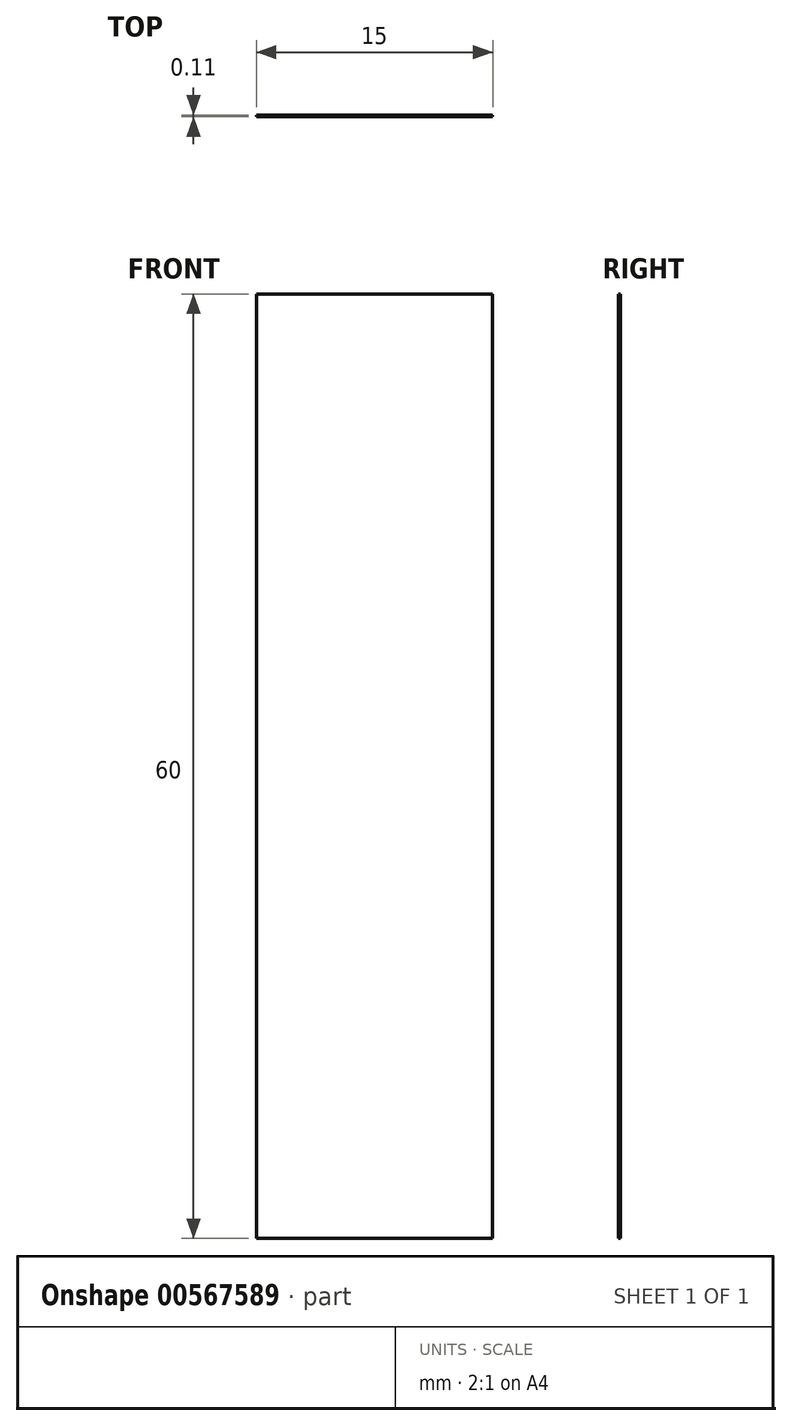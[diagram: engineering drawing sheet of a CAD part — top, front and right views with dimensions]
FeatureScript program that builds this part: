
annotation { "Feature Type Name" : "Feature", "Feature Type Description" : "" }
export const myFeature = defineFeature(function(context is Context, id is Id, definition is map)
    precondition{}
    {
        {
            var Q0;
            Q0=qCreatedBy(makeId("Front.planeOp"),FACE);
            var sketch = newSketch(context, id + "F0", { "sketchPlane" : qUnion([Q0])});
            skLineSegment(sketch, "E0.bottom", {"start": v(-59.65, -5.6) * mm, "end": v(-44.65, -5.6) * mm});
            skLineSegment(sketch, "E0.top", {"start": v(-59.65, -65.6) * mm, "end": v(-44.65, -65.6) * mm});
            skLineSegment(sketch, "E0.left", {"start": v(-59.65, -5.6) * mm, "end": v(-59.65, -65.6) * mm});
            skLineSegment(sketch, "E0.right", {"start": v(-44.65, -5.6) * mm, "end": v(-44.65, -65.6) * mm});
            skSolve(sketch);
        }
        {
            var Q0;
            Q0 = qSketchRegion(id + "F0", true);
            extrude(context, id + "F1", {"entities" : qUnion([Q0]), "depth" : 0.1 * mm, "offsetDistance" : 25 * mm});
        }
    });
